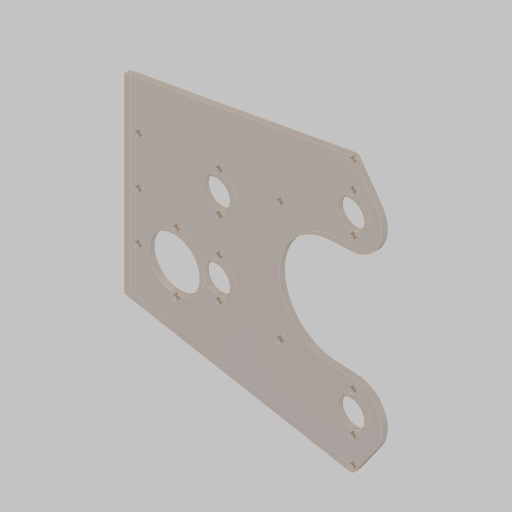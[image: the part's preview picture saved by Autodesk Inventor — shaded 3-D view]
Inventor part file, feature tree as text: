
AUTODESK INVENTOR PART (.ipt)
format: ipt  version: 2023.5 (Build 275446000, 446)  size: 192,000 bytes
history: native  units: in
note: dims shown in document units (in); Inventor stores cm internally (conversion verified against a paired STEP export)
features: sketch x1, extrude x1, hole x1
ambient origin geometry x8: Origin, YZ Plane, XZ Plane, XY Plane, X Axis, Y Axis, Z Axis, Center Point
bodies: Solid1 (feature_tree)
feature tree (3):
  sketch  "Sketch1"  dims[d0=3.0in d1=3.0in d2=4.5in d4=7.2284in d5=1.125in d6=0.75in d7=1.128in d8=1.88in d9=3.125in d10=5.6298in d11=5.992in d12=1.125in d13=0.4688in d14=0.75in d15=1.375in d16=2.3622in d18=360.0deg d20=0.25in d21=2.125in d22=1.0in d23=8.0in d24=9.5in d26=5.0in d27=0.25in d28=0.0in d29=0.375in d30=0.25in d32=1.655in d33=1.655in d34=1.655in d35=1.655in d36=1.0in d37=0.201in d38=0.75in d39=0.385in d40=0.25in d41=0.5635in d42=1.0in d43=0.8108in d44=4.0in d45=2.125in d46=2.5in]
  extrude  "Extrusion1"  Depth=0.25in
  hole  "Hole1"  [1 undecoded]
note: 1 required parameter value undecoded (feature->parameter linkage not recoverable at this tier; creation-order binding heuristic only, values carry confidence <= 0.55)
